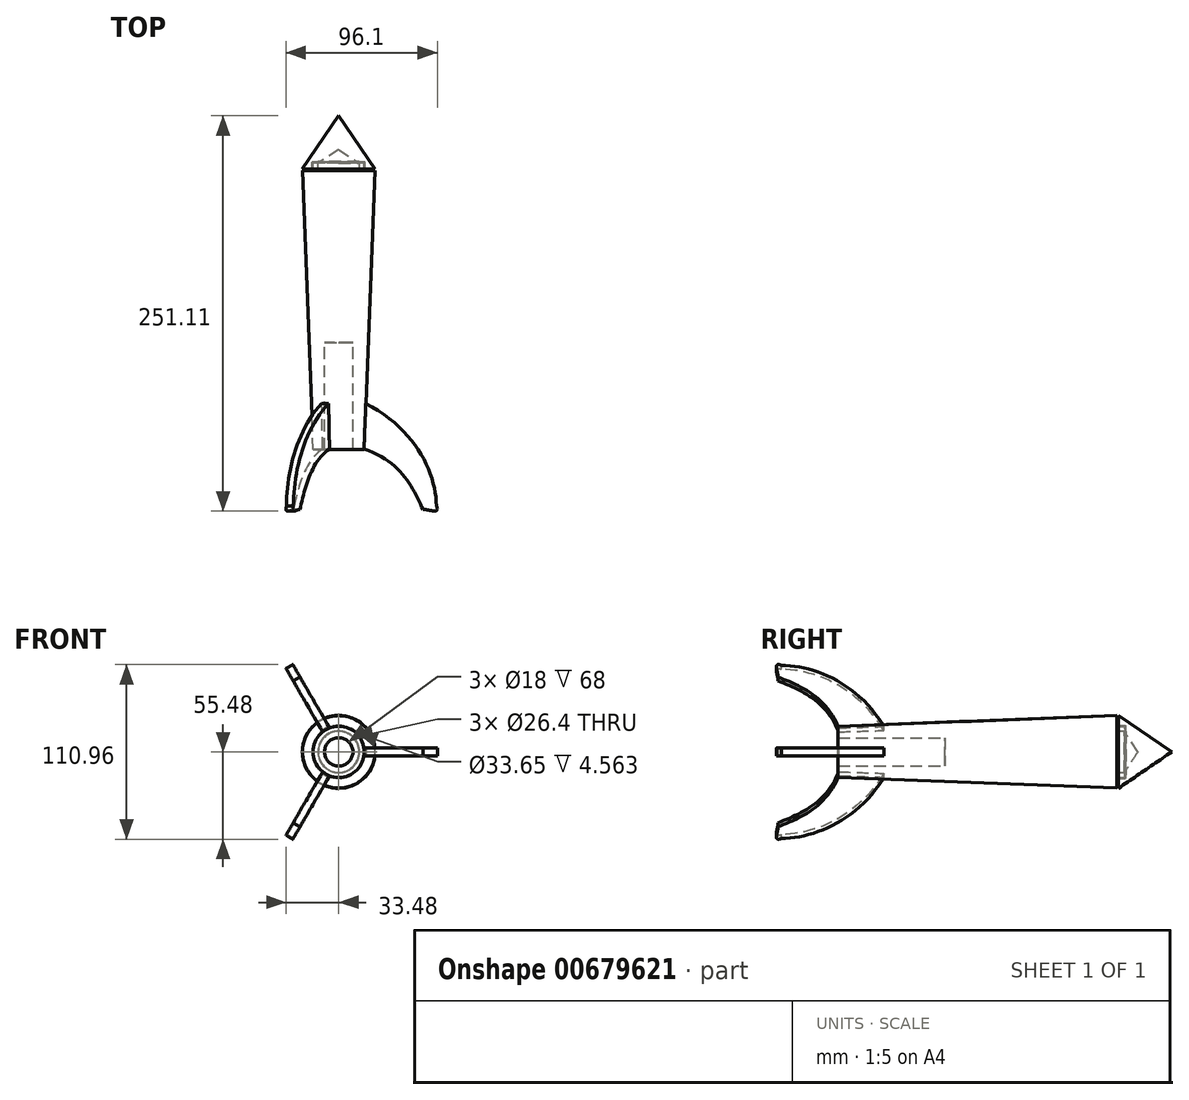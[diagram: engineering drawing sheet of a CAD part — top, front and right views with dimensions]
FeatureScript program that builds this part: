
annotation { "Feature Type Name" : "Feature", "Feature Type Description" : "" }
export const myFeature = defineFeature(function(context is Context, id is Id, definition is map)
    precondition{}
    {
        {
            var Q0;
            Q0=qCreatedBy(makeId("Top.planeOp"),FACE);
            var sketch = newSketch(context, id + "F0", { "sketchPlane" : qUnion([Q0])});
            skLineSegment(sketch, "E0", {"start": v(0, 76.2) * mm, "end": v(0, -196.27) * mm});
            skLineSegment(sketch, "E1", {"start": v(0, -27.6) * mm, "end": v(9, -27.6) * mm});
            skLineSegment(sketch, "E2", {"start": v(9, -27.6) * mm, "end": v(9, -95.6) * mm});
            skLineSegment(sketch, "E3", {"start": v(9, -95.6) * mm, "end": v(16.25, -95.6) * mm});
            skLineSegment(sketch, "E4", {"start": v(16.25, -95.6) * mm, "end": v(23, 81.73) * mm});
            skLineSegment(sketch, "E5", {"start": v(23, 81.73) * mm, "end": v(16.18, 82) * mm});
            skLineSegment(sketch, "E6", {"start": v(16.18, 82) * mm, "end": v(16.18, 86.78) * mm});
            skLineSegment(sketch, "E7", {"start": v(16.18, 86.78) * mm, "end": v(13.2, 86.9) * mm});
            skLineSegment(sketch, "E8", {"start": v(13.2, 86.9) * mm, "end": v(13.2, 82) * mm});
            skLineSegment(sketch, "E9", {"start": v(13.2, 82) * mm, "end": v(0, 82.5) * mm});
            skLineSegment(sketch, "E10", {"start": v(16.82, 86.78) * mm, "end": v(16.82, 82.54) * mm});
            skLineSegment(sketch, "E11", {"start": v(16.82, 82.54) * mm, "end": v(23.15, 82.54) * mm});
            skLineSegment(sketch, "E12", {"start": v(23.15, 82.54) * mm, "end": v(0, 116.46) * mm});
            skLineSegment(sketch, "E13", {"start": v(0, 116.46) * mm, "end": v(0, 76.2) * mm});
            skLineSegment(sketch, "E14", {"start": v(16.82, 86.78) * mm, "end": v(16.82, 87.1) * mm});
            skLineSegment(sketch, "E15", {"start": v(16.82, 87.1) * mm, "end": v(12.97, 87.25) * mm});
            skLineSegment(sketch, "E16", {"start": v(12.97, 87.25) * mm, "end": v(12.97, 86.4) * mm});
            skLineSegment(sketch, "E17", {"start": v(12.97, 86.4) * mm, "end": v(0, 94.91) * mm});
            skSolve(sketch);
        }
        {
            var Q0;
            {var subQ4=sQuery(id+"F0.wireOp",EDGE,"E1");Q0=makeQuery(id+"F0.imprint","IMPRINT",FACE,{"disambiguationData":[TD([[makeQuery(id+"F0.imprint","IMPRINT",EDGE,{"derivedFrom":subQ4}),1.0]])]});}
            var Q1;
            Q1=makeQuery(id+"F0.imprint","IMPRINT",FACE,{"disambiguationData":[TD([[makeQuery(id+"F0.imprint","IMPRINT",EDGE,{"derivedFrom":sQuery(id+"F0.wireOp",EDGE,"E10")}),1.0]])]});
            var Q2;
            Q2=sQuery(id+"F0.wireOp",EDGE,"E0");
            revolve(context, id + "F1", {"entities" : qUnion([Q0, Q1]), "axis" : qUnion([Q2]), "revolveType" : RevolveType.FULL});
        }
        {
            var Q0;
            Q0=qCreatedBy(makeId("Top.planeOp"),FACE);
            var sketch = newSketch(context, id + "F2", { "sketchPlane" : qUnion([Q0])});
            skLineSegment(sketch, "E18", {"start": v(15.95, -95.1) * mm, "end": v(17, -66.28) * mm});
            skFitSpline(sketch, "E19", {"points": [v(17, -66.28) * mm, v(62.1, -131.53) * mm], "startDerivative": vector(95.98, -49.5) * mm, "endDerivative": vector(1.35, -63.65) * mm});
            skFitSpline(sketch, "E20", {"points": [v(15.95, -95.1) * mm, v(53.51, -133.79) * mm], "startDerivative": vector(70.7, -24) * mm, "endDerivative": vector(18.96, -41.98) * mm});
            skFitSpline(sketch, "E21", {"points": [v(53.51, -133.79) * mm, v(62.1, -131.53) * mm], "startDerivative": vector(8.58, 2.26) * mm, "endDerivative": vector(-8.13, 17.6) * mm});
            skSolve(sketch);
        }
        {
            var Q0;
            Q0=makeQuery(id+"F2.imprint","IMPRINT",FACE,{"disambiguationData":[TD([[makeQuery(id+"F2.imprint","IMPRINT",EDGE,{"derivedFrom":sQuery(id+"F2.wireOp",EDGE,"E18")}),-1.0]])]});
            extrude(context, id + "F3", {"entities" : qUnion([Q0]), "operationType" : NewBodyOperationType.ADD, "depth" : 5 * mm, "offsetDistance" : 25.4 * mm, "symmetric" : true});
        }
        {
            var Q0;
            Q0=makeQuery(id+"F1.opRevolve","SWEPT_BODY",BODY,{"disambiguationData":[OSD([sQuery(id+"F0.wireOp",EDGE,"E0"),sQuery(id+"F0.wireOp",EDGE,"E1"),sQuery(id+"F0.wireOp",EDGE,"E2"),sQuery(id+"F0.wireOp",EDGE,"E3"),sQuery(id+"F0.wireOp",EDGE,"E4"),sQuery(id+"F0.wireOp",EDGE,"E5"),sQuery(id+"F0.wireOp",EDGE,"E6"),sQuery(id+"F0.wireOp",EDGE,"E7"),sQuery(id+"F0.wireOp",EDGE,"E8"),sQuery(id+"F0.wireOp",EDGE,"E9"),sQuery(id+"F0.wireOp",EDGE,"E13")])]});
            var Q1;
            Q1=sQuery(id+"F0.wireOp",EDGE,"E0");
            circularPattern(context, id + "F4", {"entities" : qUnion([Q0]), "axis" : qUnion([Q1]), "angle" : 360 * degree, "instanceCount" : 3, "equalSpace" : true});
        }
    });
